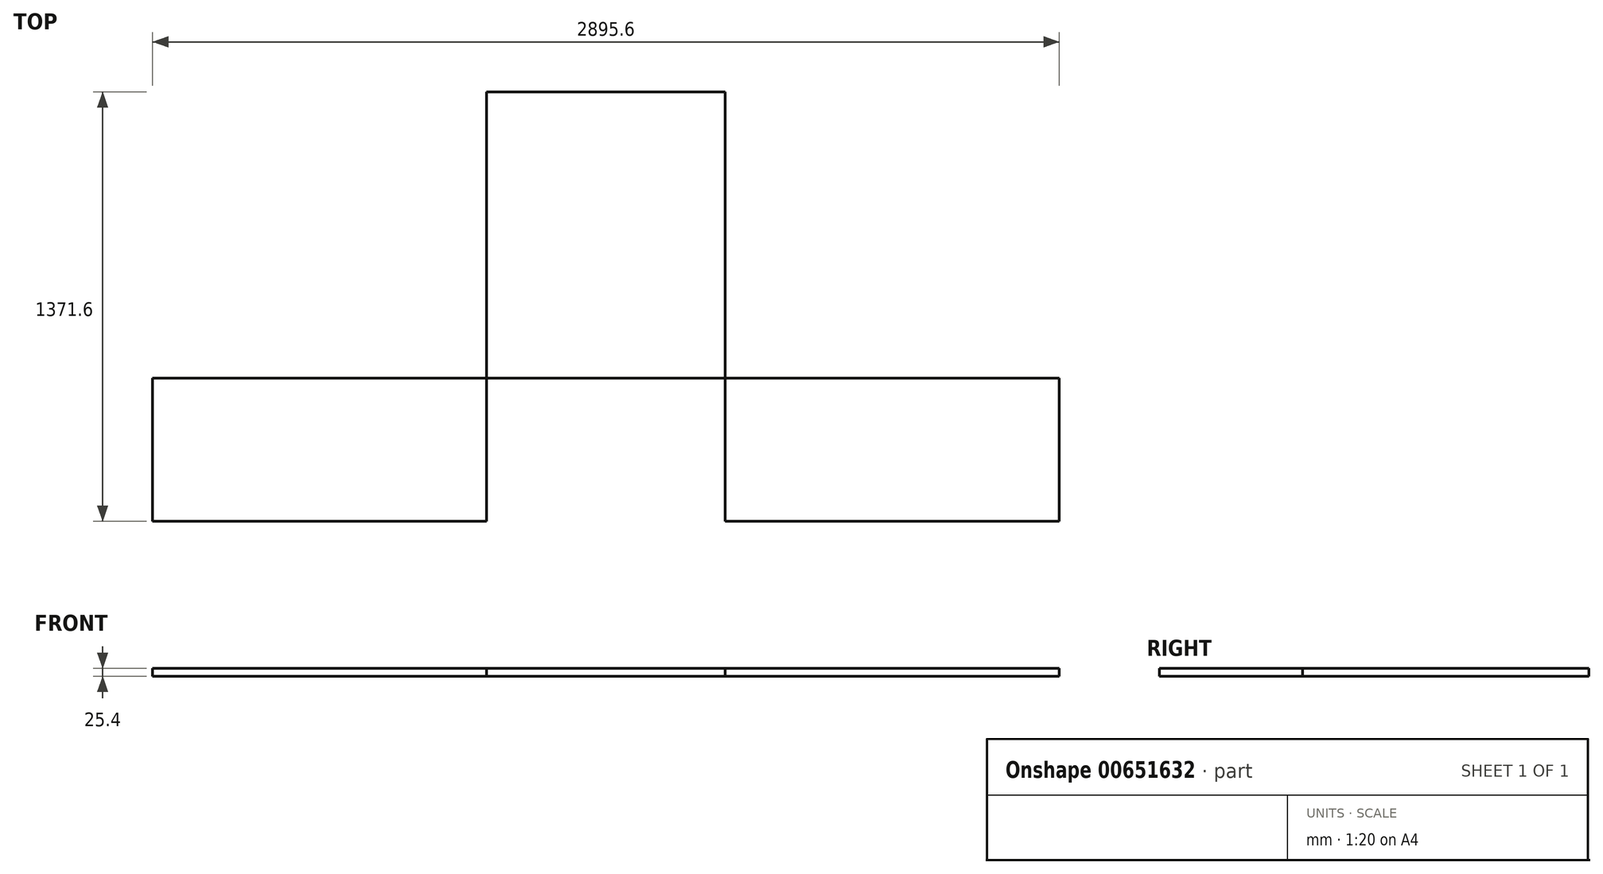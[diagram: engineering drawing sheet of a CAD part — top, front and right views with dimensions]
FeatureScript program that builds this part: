
annotation { "Feature Type Name" : "Feature", "Feature Type Description" : "" }
export const myFeature = defineFeature(function(context is Context, id is Id, definition is map)
    precondition{}
    {
        {
            var Q0;
            Q0=qCreatedBy(makeId("Top.planeOp"),FACE);
            var sketch = newSketch(context, id + "F0", { "sketchPlane" : qUnion([Q0])});
            skLineSegment(sketch, "E0.bottom", {"start": v(0, 914.4) * mm, "end": v(762, 914.4) * mm});
            skLineSegment(sketch, "E0.top", {"start": v(0, 0) * mm, "end": v(762, 0) * mm});
            skLineSegment(sketch, "E0.left", {"start": v(0, 914.4) * mm, "end": v(0, 0) * mm});
            skLineSegment(sketch, "E0.right", {"start": v(762, 914.4) * mm, "end": v(762, 0) * mm});
            skLineSegment(sketch, "E1.bottom", {"start": v(0, 0) * mm, "end": v(-1066.8, 0) * mm});
            skLineSegment(sketch, "E1.top", {"start": v(0, -457.2) * mm, "end": v(-1066.8, -457.2) * mm});
            skLineSegment(sketch, "E1.left", {"start": v(0, 0) * mm, "end": v(0, -457.2) * mm});
            skLineSegment(sketch, "E1.right", {"start": v(-1066.8, 0) * mm, "end": v(-1066.8, -457.2) * mm});
            skLineSegment(sketch, "E2.bottom", {"start": v(762, 0) * mm, "end": v(1828.8, 0) * mm});
            skLineSegment(sketch, "E2.top", {"start": v(762, -457.2) * mm, "end": v(1828.8, -457.2) * mm});
            skLineSegment(sketch, "E2.left", {"start": v(762, 0) * mm, "end": v(762, -457.2) * mm});
            skLineSegment(sketch, "E2.right", {"start": v(1828.8, 0) * mm, "end": v(1828.8, -457.2) * mm});
            skSolve(sketch);
        }
        {
            var Q0;
            Q0 = qSketchRegion(id + "F0", true);
            extrude(context, id + "F1", {"entities" : qUnion([Q0]), "depth" : 25.4 * mm, "offsetDistance" : 25.4 * mm});
        }
    });
